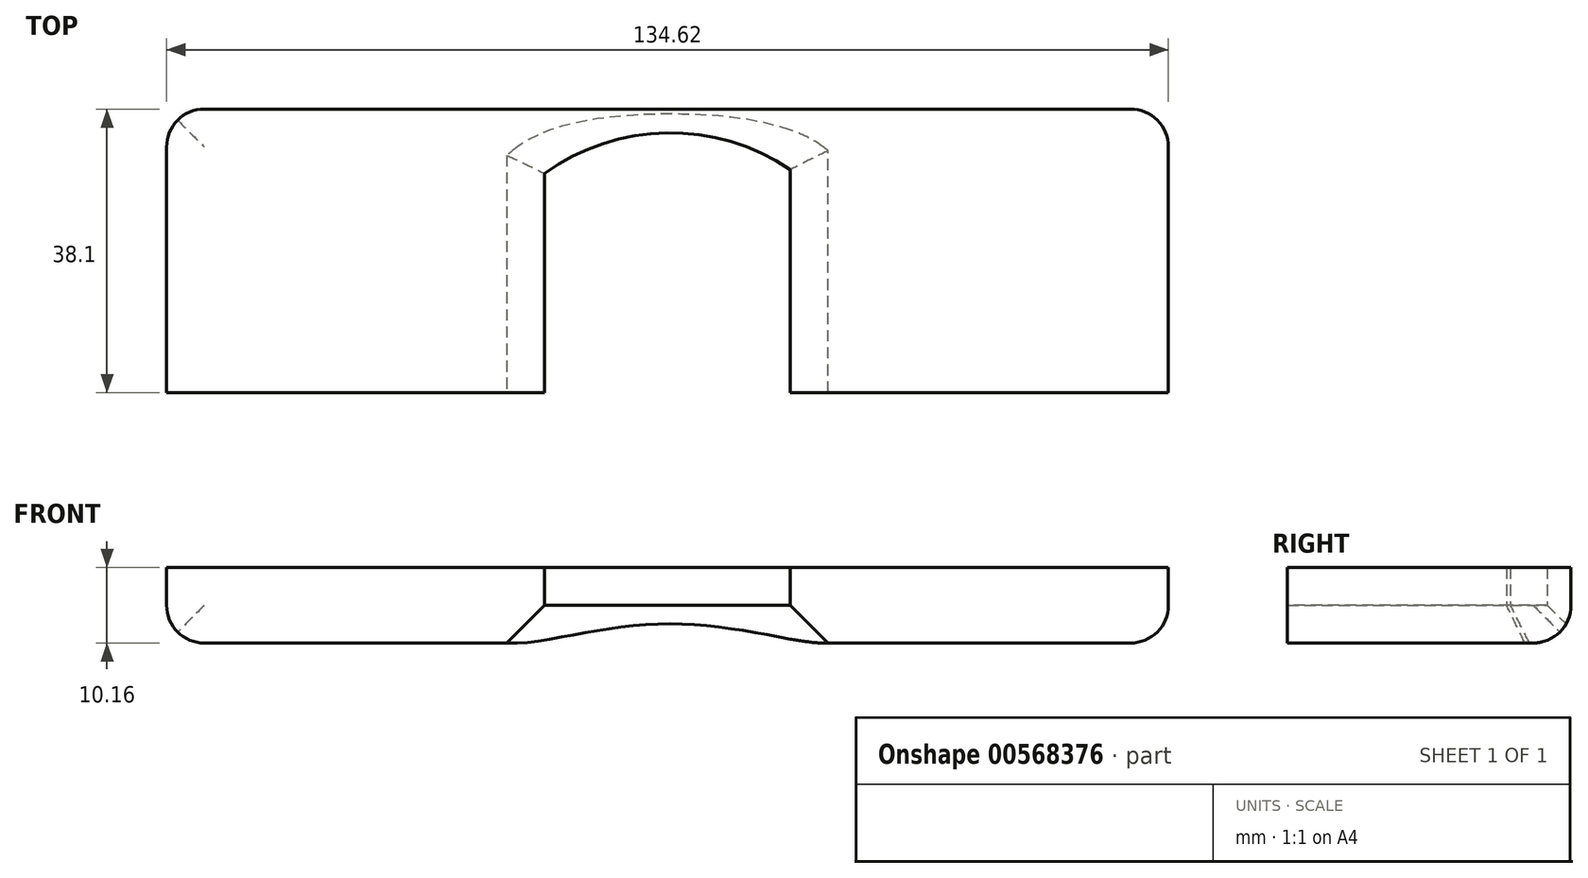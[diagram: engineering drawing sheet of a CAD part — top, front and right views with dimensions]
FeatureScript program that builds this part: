
annotation { "Feature Type Name" : "Feature", "Feature Type Description" : "" }
export const myFeature = defineFeature(function(context is Context, id is Id, definition is map)
    precondition{}
    {
        {
            var Q0;
            Q0=qCreatedBy(makeId("Top.planeOp"),FACE);
            var sketch = newSketch(context, id + "F0", { "sketchPlane" : qUnion([Q0])});
            skLineSegment(sketch, "E0.bottom", {"start": v(-42.41, 21.08) * mm, "end": v(8.39, 21.08) * mm});
            skLineSegment(sketch, "E0.top", {"start": v(-42.41, -17.02) * mm, "end": v(8.39, -17.02) * mm});
            skLineSegment(sketch, "E0.left", {"start": v(-42.41, 21.08) * mm, "end": v(-42.41, -17.02) * mm});
            skLineSegment(sketch, "E0.right", {"start": v(8.39, 21.08) * mm, "end": v(8.39, -17.02) * mm});
            skLineSegment(sketch, "E1.bottom", {"start": v(41.4, 21.08) * mm, "end": v(92.2, 21.08) * mm});
            skLineSegment(sketch, "E1.top", {"start": v(41.4, -17.02) * mm, "end": v(92.2, -17.02) * mm});
            skLineSegment(sketch, "E1.left", {"start": v(41.4, 21.08) * mm, "end": v(41.4, -17.02) * mm});
            skLineSegment(sketch, "E1.right", {"start": v(92.2, 21.08) * mm, "end": v(92.2, -17.02) * mm});
            skLineSegment(sketch, "E2", {"start": v(8.39, 21.08) * mm, "end": v(41.4, 21.08) * mm});
            skArc(sketch, "E3", {"start": v(41.4, 12.94) * mm, "mid": v(24.81, 17.9) * mm, "end": v(8.39, 12.42) * mm});
            skSolve(sketch);
        }
        {
            var Q0;
            {var subQ1=sQuery(id+"F0.wireOp",EDGE,"E0.bottom");Q0=makeQuery(id+"F0.imprint","IMPRINT",FACE,{"disambiguationData":[TD([[makeQuery(id+"F0.imprint","IMPRINT",EDGE,{"derivedFrom":subQ1}),-1.0]])]});}
            var Q1;
            {var subQ0=sQuery(id+"F0.wireOp",EDGE,"E2");Q1=makeQuery(id+"F0.imprint","IMPRINT",FACE,{"disambiguationData":[TD([[makeQuery(id+"F0.imprint","IMPRINT",EDGE,{"derivedFrom":subQ0}),-1.0]])]});}
            var Q2;
            {var subQ3=sQuery(id+"F0.wireOp",EDGE,"E1.bottom");Q2=makeQuery(id+"F0.imprint","IMPRINT",FACE,{"disambiguationData":[TD([[makeQuery(id+"F0.imprint","IMPRINT",EDGE,{"derivedFrom":subQ3}),-1.0]])]});}
            extrude(context, id + "F1", {"entities" : qUnion([Q0, Q1, Q2]), "depth" : 10.16 * mm, "offsetDistance" : 25.4 * mm});
        }
        {
            var Q0;
            Q0=makeQuery(id+"F1.opExtrude","CAP_EDGE",EDGE,{"disambiguationData":[OSD([sQuery(id+"F0.wireOp",EDGE,"E1.left")])],"isStart":true});
            var Q1;
            Q1=makeQuery(id+"F1.opExtrude","CAP_EDGE",EDGE,{"disambiguationData":[OSD([sQuery(id+"F0.wireOp",EDGE,"E0.right")])],"isStart":true});
            var Q2;
            Q2=makeQuery(id+"F1.opExtrude","CAP_EDGE",EDGE,{"disambiguationData":[OSD([sQuery(id+"F0.wireOp",EDGE,"E3")])],"isStart":true});
            chamfer(context, id + "F2", {"entities" : qUnion([Q0, Q1, Q2]), "width" : 5.08 * mm, "tangentPropagation" : true});
        }
        {
            var Q0;
            Q0=makeQuery(id+"F1.opExtrude","SWEPT_EDGE",EDGE,{"disambiguationData":[OSD([sQuery(id+"F0.wireOp",EDGE,"E1.bottom"),sQuery(id+"F0.wireOp",EDGE,"E1.right")])]});
            var Q1;
            Q1=makeQuery(id+"F1.opExtrude","CAP_EDGE",EDGE,{"disambiguationData":[OSD([sQuery(id+"F0.wireOp",EDGE,"E1.bottom")])],"isStart":true});
            var Q2;
            Q2=makeQuery(id+"F1.opExtrude","CAP_EDGE",EDGE,{"disambiguationData":[OSD([sQuery(id+"F0.wireOp",EDGE,"E1.right")])],"isStart":true});
            var Q3;
            Q3=makeQuery(id+"F1.opExtrude","CAP_EDGE",EDGE,{"disambiguationData":[OSD([sQuery(id+"F0.wireOp",EDGE,"E0.left")])],"isStart":true});
            var Q4;
            Q4=makeQuery(id+"F1.opExtrude","SWEPT_EDGE",EDGE,{"disambiguationData":[OSD([sQuery(id+"F0.wireOp",EDGE,"E0.bottom"),sQuery(id+"F0.wireOp",EDGE,"E0.left")])]});
            fillet(context, id + "F3", {"entities" : qUnion([Q0, Q1, Q2, Q3, Q4]), "radius" : 5.08 * mm, "tangentPropagation" : true, "allowEdgeOverflow" : false});
        }
    });
